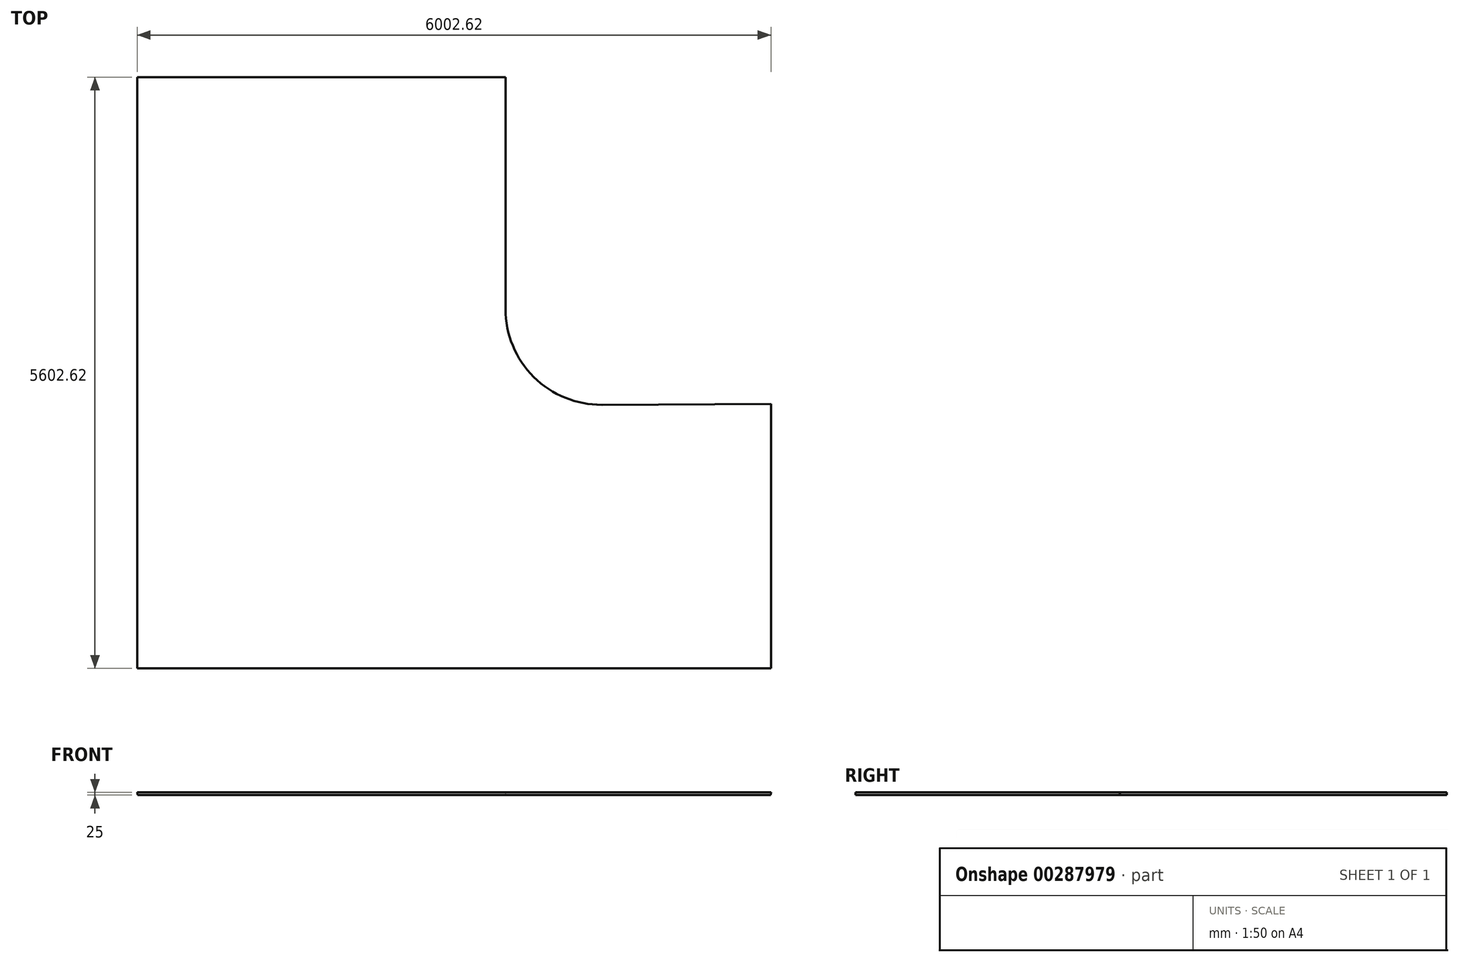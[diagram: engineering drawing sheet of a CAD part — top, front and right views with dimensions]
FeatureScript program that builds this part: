
annotation { "Feature Type Name" : "Feature", "Feature Type Description" : "" }
export const myFeature = defineFeature(function(context is Context, id is Id, definition is map)
    precondition{}
    {
        {
            var Q0;
            Q0=qCreatedBy(makeId("Top.planeOp"),FACE);
            var sketch = newSketch(context, id + "F0", { "sketchPlane" : qUnion([Q0])});
            skLineSegment(sketch, "E0", {"start": v(-2943.51, -1000.58) * mm, "end": v(3056.49, -1000.58) * mm});
            skLineSegment(sketch, "E1", {"start": v(-2943.51, -1000.58) * mm, "end": v(-2943.51, 4599.42) * mm});
            skLineSegment(sketch, "E2", {"start": v(-2943.51, 4599.42) * mm, "end": v(541.49, 4599.42) * mm});
            skLineSegment(sketch, "E3", {"start": v(3056.49, -1000.58) * mm, "end": v(3056.49, 1504.42) * mm});
            skLineSegment(sketch, "E4", {"start": v(541.49, 4599.42) * mm, "end": v(541.49, 2404.42) * mm});
            skLineSegment(sketch, "E5", {"start": v(1457.17, 1494.43) * mm, "end": v(3056.49, 1504.42) * mm});
            skPoint(sketch, "E6.visualSharp", {"position": v(541.49, 1488.72) * mm});
            skArc(sketch, "E6.filletArc", {"start": v(541.49, 2404.42) * mm, "mid": v(810.03, 1758.94) * mm, "end": v(1457.17, 1494.43) * mm});
            skLineSegment(sketch, "E7", {"start": v(541.49, 4599.42) * mm, "end": v(1441.49, 4599.42) * mm});
            skLineSegment(sketch, "E8", {"start": v(541.49, 4599.42) * mm, "end": v(991.49, 4599.42) * mm});
            skLineSegment(sketch, "E9", {"start": v(991.49, 4599.42) * mm, "end": v(991.49, 2409.42) * mm});
            skLineSegment(sketch, "E10", {"start": v(1441.49, 4599.42) * mm, "end": v(1451.49, 2404.42) * mm});
            skLineSegment(sketch, "E11", {"start": v(3056.49, 1504.42) * mm, "end": v(3056.49, 2404.42) * mm});
            skLineSegment(sketch, "E12", {"start": v(3056.49, 2404.42) * mm, "end": v(1451.49, 2404.42) * mm});
            skLineSegment(sketch, "E13", {"start": v(3056.49, 1954.42) * mm, "end": v(1446.49, 1954.42) * mm});
            skPoint(sketch, "E14.newPointB", {"position": v(1451.49, 1954.42) * mm});
            skArc(sketch, "E14.filletArc", {"start": v(991.49, 2409.42) * mm, "mid": v(1124.75, 2087.68) * mm, "end": v(1446.49, 1954.42) * mm});
            skLineSegment(sketch, "E15", {"start": v(1441.49, 4599.42) * mm, "end": v(1442.8, 4309.42) * mm});
            skLineSegment(sketch, "E16", {"start": v(1442.8, 4309.42) * mm, "end": v(541.49, 4305.31) * mm});
            skLineSegment(sketch, "E17", {"start": v(1442.8, 4309.42) * mm, "end": v(1444.13, 4019.42) * mm});
            skLineSegment(sketch, "E18", {"start": v(1444.13, 4019.42) * mm, "end": v(1445.45, 3729.42) * mm});
            skLineSegment(sketch, "E19", {"start": v(1445.45, 3729.42) * mm, "end": v(1446.77, 3439.42) * mm});
            skLineSegment(sketch, "E20", {"start": v(1446.77, 3439.42) * mm, "end": v(1448.1, 3149.42) * mm});
            skLineSegment(sketch, "E21", {"start": v(1448.1, 3149.42) * mm, "end": v(1449.41, 2859.42) * mm});
            skLineSegment(sketch, "E22", {"start": v(1444.13, 4019.42) * mm, "end": v(541.49, 4015.3) * mm});
            skLineSegment(sketch, "E23", {"start": v(1445.45, 3729.42) * mm, "end": v(541.49, 3725.3) * mm});
            skLineSegment(sketch, "E24", {"start": v(1446.77, 3439.42) * mm, "end": v(541.49, 3435.3) * mm});
            skLineSegment(sketch, "E25", {"start": v(1448.1, 3149.42) * mm, "end": v(541.49, 3145.29) * mm});
            skLineSegment(sketch, "E26", {"start": v(1449.41, 2859.42) * mm, "end": v(541.49, 2855.28) * mm});
            skLineSegment(sketch, "E27", {"start": v(3056.49, 2404.42) * mm, "end": v(2766.49, 2404.42) * mm});
            skLineSegment(sketch, "E28", {"start": v(2766.49, 2404.42) * mm, "end": v(2476.49, 2404.42) * mm});
            skLineSegment(sketch, "E29", {"start": v(2476.49, 2404.42) * mm, "end": v(2186.49, 2404.42) * mm});
            skLineSegment(sketch, "E30", {"start": v(2186.49, 2404.42) * mm, "end": v(1896.49, 2404.42) * mm});
            skLineSegment(sketch, "E31", {"start": v(2766.49, 2404.42) * mm, "end": v(2766.49, 1502.6) * mm});
            skLineSegment(sketch, "E32", {"start": v(2476.49, 2404.42) * mm, "end": v(2476.49, 1500.8) * mm});
            skLineSegment(sketch, "E33", {"start": v(2186.49, 2404.42) * mm, "end": v(2186.49, 1498.99) * mm});
            skLineSegment(sketch, "E34", {"start": v(1896.49, 2404.42) * mm, "end": v(1896.49, 1497.18) * mm});
            skLineSegment(sketch, "E35", {"start": v(1441.49, 4599.42) * mm, "end": v(1491.49, 4599.64) * mm});
            skLineSegment(sketch, "E36", {"start": v(1491.49, 4599.64) * mm, "end": v(1501.26, 2454.42) * mm});
            skLineSegment(sketch, "E37", {"start": v(3056.49, 2404.42) * mm, "end": v(3056.26, 2454.42) * mm});
            skLineSegment(sketch, "E38", {"start": v(3056.26, 2454.42) * mm, "end": v(1501.26, 2454.42) * mm});
            skSolve(sketch);
        }
        {
            var Q0;
            Q0=makeQuery(id+"F0.imprint","IMPRINT",FACE,{"disambiguationData":[TD([[makeQuery(id+"F0.imprint","IMPRINT",EDGE,{"derivedFrom":sQuery(id+"F0.wireOp",EDGE,"E0")}),1.0]])]});
            extrude(context, id + "F1", {"entities" : qUnion([Q0]), "depth" : 25 * mm, "hasDraft" : true, "draftAngle" : 3 * degree});
        }
    });
